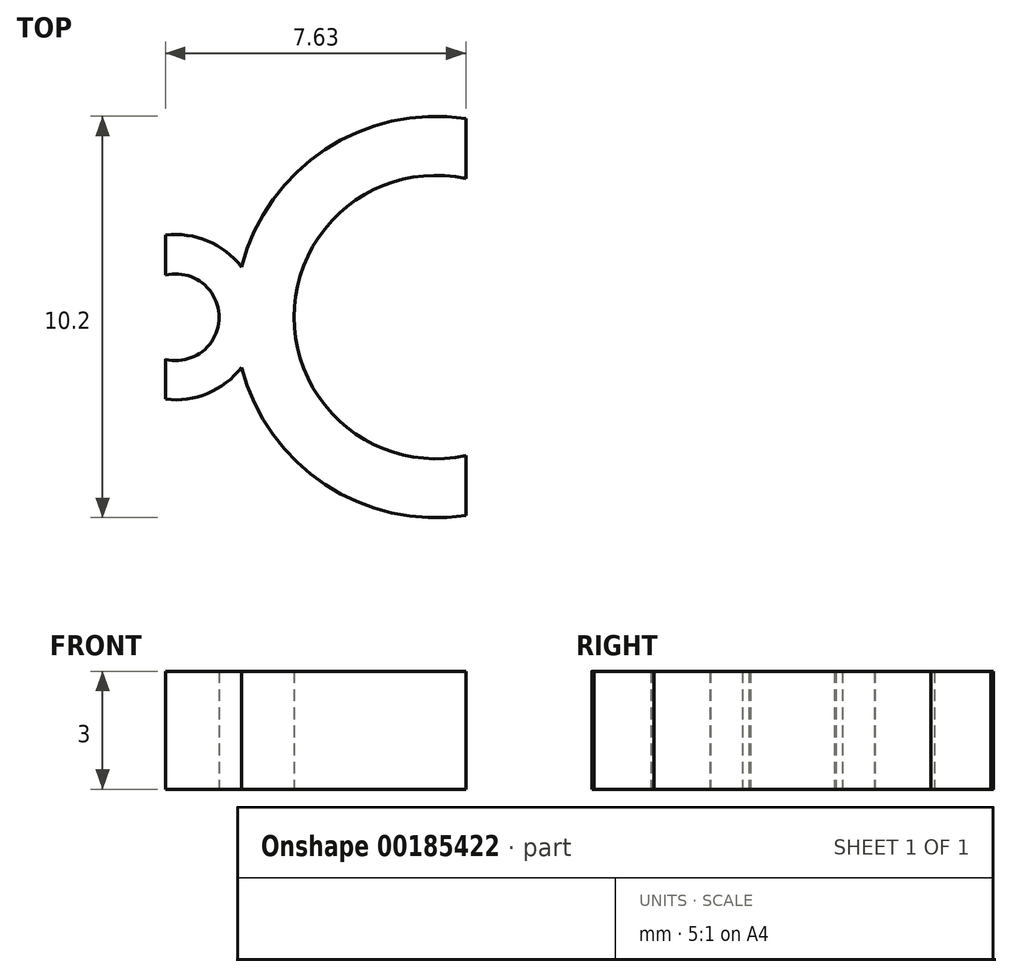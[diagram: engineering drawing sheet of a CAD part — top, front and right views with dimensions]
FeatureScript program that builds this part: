
annotation { "Feature Type Name" : "Feature", "Feature Type Description" : "" }
export const myFeature = defineFeature(function(context is Context, id is Id, definition is map)
    precondition{}
    {
        {
            var Q0;
            Q0=qCreatedBy(makeId("Top.planeOp"),FACE);
            var sketch = newSketch(context, id + "F0", { "sketchPlane" : qUnion([Q0])});
            skArc(sketch, "E0", {"start": v(-3.57, -0.84) * mm, "mid": v(-7.94, -4.35) * mm, "end": v(-3.57, -7.87) * mm});
            skArc(sketch, "E1", {"start": v(-3.57, 0.69) * mm, "mid": v(-7.15, -0.1) * mm, "end": v(-9.27, -3.08) * mm});
            skLineSegment(sketch, "E2", {"start": v(-3.57, -9.4) * mm, "end": v(-3.57, -7.87) * mm});
            skArc(sketch, "E3", {"start": v(-11.2, -5.42) * mm, "mid": v(-9.84, -4.36) * mm, "end": v(-11.2, -3.29) * mm});
            skArc(sketch, "E4", {"start": v(-9.27, -3.08) * mm, "mid": v(-10.13, -2.42) * mm, "end": v(-11.2, -2.27) * mm});
            skArc(sketch, "E5.trimOffspring", {"start": v(-9.27, -5.63) * mm, "mid": v(-7.14, -8.6) * mm, "end": v(-3.57, -9.4) * mm});
            skLineSegment(sketch, "E6", {"start": v(-11.2, -6.44) * mm, "end": v(-11.2, -5.42) * mm});
            skLineSegment(sketch, "E7.trimOffspring", {"start": v(-3.57, -0.84) * mm, "end": v(-3.57, 0.69) * mm});
            skArc(sketch, "E8.trimOffspring", {"start": v(-11.2, -6.44) * mm, "mid": v(-10.13, -6.3) * mm, "end": v(-9.27, -5.63) * mm});
            skLineSegment(sketch, "E9.trimOffspring", {"start": v(-11.2, -3.29) * mm, "end": v(-11.2, -2.27) * mm});
            skSolve(sketch);
        }
        {
            var Q0;
            Q0=makeQuery(id+"F0.imprint","IMPRINT",FACE,{"disambiguationData":[TD([[makeQuery(id+"F0.imprint","IMPRINT",EDGE,{"derivedFrom":sQuery(id+"F0.wireOp",EDGE,"E0")}),-1.0]])]});
            extrude(context, id + "F1", {"entities" : qUnion([Q0]), "depth" : 3 * mm});
        }
    });
